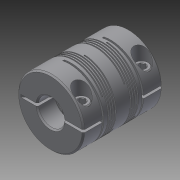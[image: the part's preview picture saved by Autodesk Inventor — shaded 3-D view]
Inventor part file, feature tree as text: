
AUTODESK INVENTOR PART (.ipt)
format: ipt  version: 2015 (Build 190159000, 159)  size: 2,531,840 bytes
history: native  units: in
note: dims shown in document units (in); Inventor stores cm internally (conversion verified against a paired STEP export)
features: imported_body x3, boolean_combine x2, other x1, mirror x1
ambient origin geometry x8: Origin, YZ Plane, XZ Plane, XY Plane, X Axis, Y Axis, Z Axis, Center Point
bodies: Body1 (feature_tree), Body2 (feature_tree), Body3 (feature_tree)
feature tree (7):
  boolean_combine  "Combine3"
  other  "2464K2201"
  mirror  "Mirror1[2]"
  boolean_combine  "Combine4"
  imported_body  "Base1"
  imported_body  "Base2"
  imported_body  "Base3"
